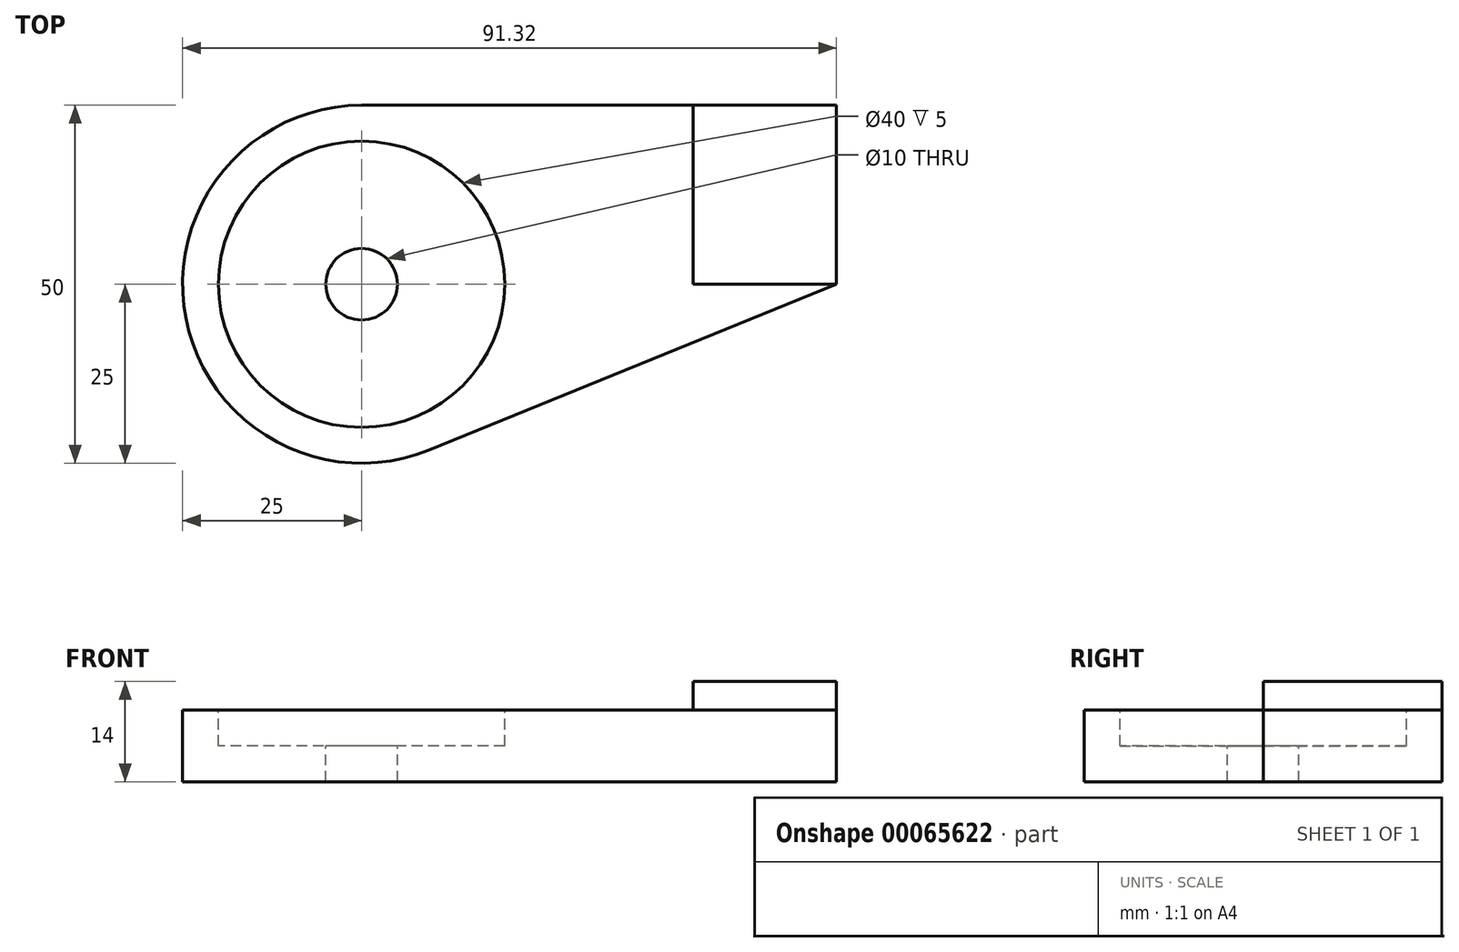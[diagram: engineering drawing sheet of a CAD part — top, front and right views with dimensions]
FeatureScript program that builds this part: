
annotation { "Feature Type Name" : "Feature", "Feature Type Description" : "" }
export const myFeature = defineFeature(function(context is Context, id is Id, definition is map)
    precondition{}
    {
        {
            var Q0;
            Q0=qCreatedBy(makeId("Top.planeOp"),FACE);
            var sketch = newSketch(context, id + "F0", { "sketchPlane" : qUnion([Q0])});
            skCircle(sketch, "E0", {"center": v(0, 0) * mm, "radius": 25 * mm});
            skLineSegment(sketch, "E1", {"start": v(0, 25) * mm, "end": v(66.32, 25) * mm});
            skLineSegment(sketch, "E2", {"start": v(66.32, 25) * mm, "end": v(66.32, 0) * mm});
            skLineSegment(sketch, "E3", {"start": v(66.32, 0) * mm, "end": v(9.42, -23.16) * mm});
            skSolve(sketch);
        }
        {
            var Q0;
            Q0 = qSketchRegion(id + "F0", true);
            var Q1;
            {var subQ0=sQuery(id+"F0.wireOp",EDGE,"E0");var subQ1=makeQuery(id+"F0.imprint","INTERSECT",VERTEX,{"derivedFrom":[subQ0,sQuery(id+"F0.wireOp",EDGE,"E1")]});Q1=makeQuery(id+"F0.imprint","IMPRINT",FACE,{"disambiguationData":[TD([[makeQuery(id+"F0.imprint","IMPRINT",EDGE,{"disambiguationData":[TD([[subQ1,-1.0]])],"derivedFrom":subQ0}),1.0]])]});}
            var Q2;
            {var subQ0=sQuery(id+"F0.wireOp",EDGE,"E1");Q2=makeQuery(id+"F0.imprint","IMPRINT",FACE,{"disambiguationData":[TD([[makeQuery(id+"F0.imprint","IMPRINT",EDGE,{"derivedFrom":subQ0}),-1.0]])]});}
            extrude(context, id + "F1", {"entities" : qUnion([Q0, Q1, Q2]), "depth" : 10 * mm});
        }
        {
            var Q0;
            Q0=makeQuery(id+"F1.opExtrude","CAP_FACE",FACE,{"disambiguationData":[OSD([sQuery(id+"F0.wireOp",EDGE,"E0"),sQuery(id+"F0.wireOp",EDGE,"E1"),sQuery(id+"F0.wireOp",EDGE,"E2"),sQuery(id+"F0.wireOp",EDGE,"E3")])],"isStart":false});
            var sketch = newSketch(context, id + "F2", { "sketchPlane" : qUnion([Q0])});
            skCircle(sketch, "E4", {"center": v(0, 0) * mm, "radius": 20 * mm});
            skSolve(sketch);
        }
        {
            var Q0;
            Q0 = qSketchRegion(id + "F2", true);
            var Q1;
            Q1=makeQuery(id+"F2.imprint","IMPRINT",FACE,{"disambiguationData":[TD([[makeQuery(id+"F2.imprint","IMPRINT",EDGE,{"derivedFrom":sQuery(id+"F2.wireOp",EDGE,"E4")}),1.0]])]});
            extrude(context, id + "F3", {"entities" : qUnion([Q0, Q1]), "operationType" : NewBodyOperationType.REMOVE, "oppositeDirection" : true, "depth" : 5 * mm});
        }
        {
            var Q0;
            Q0=makeQuery(id+"F3.boolean.opBoolean","COPY",FACE,{"derivedFrom":makeQuery(id+"F3.opExtrude","CAP_FACE",FACE,{"disambiguationData":[OSD([sQuery(id+"F2.wireOp",EDGE,"E4")])],"isStart":false})});
            var sketch = newSketch(context, id + "F4", { "sketchPlane" : qUnion([Q0])});
            skCircle(sketch, "E5", {"center": v(0, 0) * mm, "radius": 5 * mm});
            skSolve(sketch);
        }
        {
            var Q0;
            Q0=makeQuery(id+"F4.imprint","IMPRINT",FACE,{"disambiguationData":[TD([[makeQuery(id+"F4.imprint","IMPRINT",EDGE,{"derivedFrom":sQuery(id+"F4.wireOp",EDGE,"E5")}),1.0]])]});
            extrude(context, id + "F5", {"entities" : qUnion([Q0]), "operationType" : NewBodyOperationType.REMOVE, "oppositeDirection" : true, "depth" : 25 * mm});
        }
        {
            var Q0;
            Q0=makeQuery(id+"F1.opExtrude","CAP_FACE",FACE,{"disambiguationData":[OSD([sQuery(id+"F0.wireOp",EDGE,"E0"),sQuery(id+"F0.wireOp",EDGE,"E1"),sQuery(id+"F0.wireOp",EDGE,"E2"),sQuery(id+"F0.wireOp",EDGE,"E3")])],"isStart":false});
            var sketch = newSketch(context, id + "F6", { "sketchPlane" : qUnion([Q0])});
            skLineSegment(sketch, "E6.bottom", {"start": v(66.32, 25) * mm, "end": v(46.32, 25) * mm});
            skLineSegment(sketch, "E6.top", {"start": v(66.32, 0) * mm, "end": v(46.32, 0) * mm});
            skLineSegment(sketch, "E6.left", {"start": v(66.32, 25) * mm, "end": v(66.32, 0) * mm});
            skLineSegment(sketch, "E6.right", {"start": v(46.32, 25) * mm, "end": v(46.32, 0) * mm});
            skSolve(sketch);
        }
        {
            var Q0;
            Q0=makeQuery(id+"F6.imprint","IMPRINT",FACE,{"disambiguationData":[TD([[makeQuery(id+"F6.imprint","IMPRINT",EDGE,{"derivedFrom":sQuery(id+"F6.wireOp",EDGE,"E6.bottom")}),-1.0]])]});
            extrude(context, id + "F7", {"entities" : qUnion([Q0]), "depth" : 4 * mm});
        }
    });
